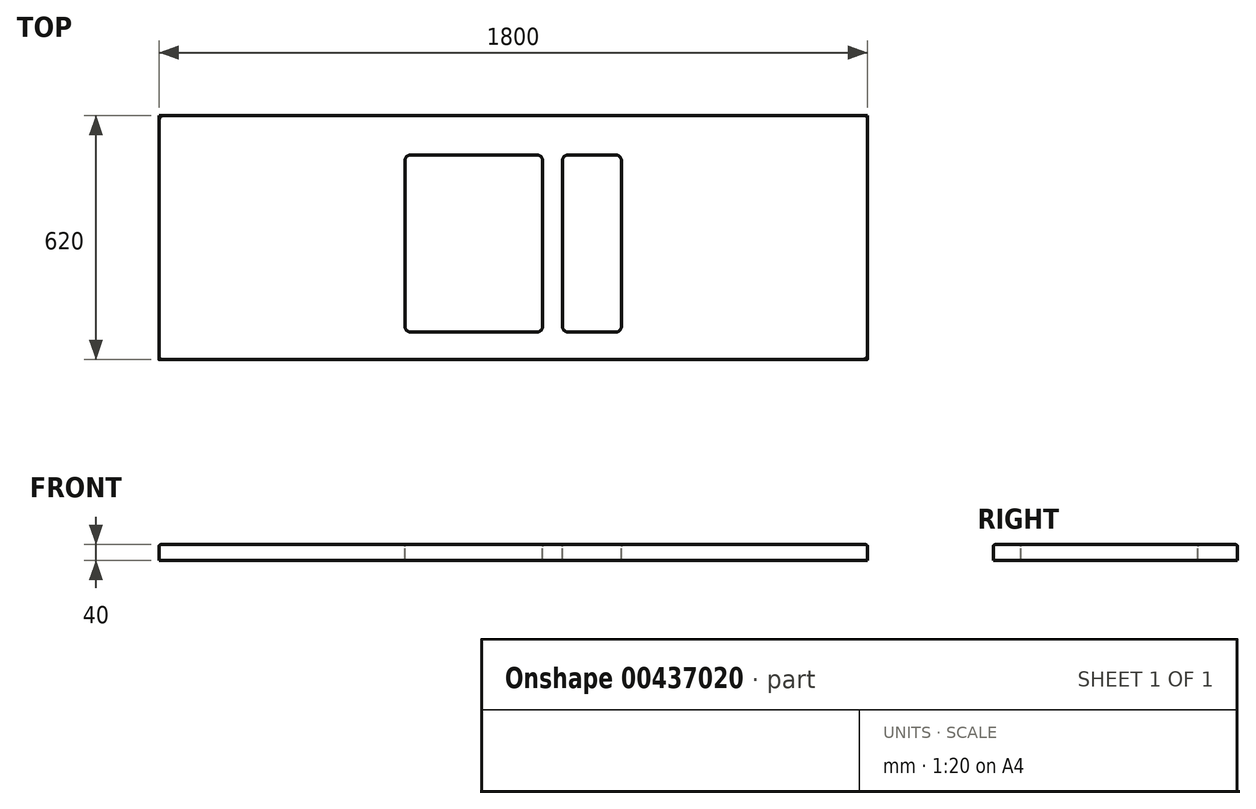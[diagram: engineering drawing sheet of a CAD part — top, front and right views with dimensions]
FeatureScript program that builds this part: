
annotation { "Feature Type Name" : "Feature", "Feature Type Description" : "" }
export const myFeature = defineFeature(function(context is Context, id is Id, definition is map)
    precondition{}
    {
        {
            var Q0;
            Q0=qCreatedBy(makeId("Right.planeOp"),FACE);
            var sketch = newSketch(context, id + "F0", { "sketchPlane" : qUnion([Q0])});
            skLineSegment(sketch, "E0.bottom", {"start": v(0, 0) * mm, "end": v(-620, 0) * mm});
            skLineSegment(sketch, "E0.top", {"start": v(0, 40) * mm, "end": v(-620, 40) * mm});
            skLineSegment(sketch, "E0.left", {"start": v(0, 0) * mm, "end": v(0, 40) * mm});
            skLineSegment(sketch, "E0.right", {"start": v(-620, 0) * mm, "end": v(-620, 40) * mm});
            skSolve(sketch);
        }
        {
            var Q0;
            Q0=qSketchRegion(id+"F0",true);
            extrude(context, id + "F1", {"entities" : qUnion([Q0]), "depth" : 1800 * mm});
        }
        {
            var Q0;
            Q0=makeQuery(id+"F1.opExtrude","SWEPT_FACE",FACE,{"disambiguationData":[OSD([sQuery(id+"F0.wireOp",EDGE,"E0.top")])]});
            var sketch = newSketch(context, id + "F2", { "sketchPlane" : qUnion([Q0])});
            skLineSegment(sketch, "E1.bottom", {"start": v(640, -100) * mm, "end": v(960, -100) * mm});
            skLineSegment(sketch, "E1.top", {"start": v(640, -550) * mm, "end": v(960, -550) * mm});
            skLineSegment(sketch, "E1.left", {"start": v(625, -115) * mm, "end": v(625, -535) * mm});
            skLineSegment(sketch, "E1.right", {"start": v(975, -115) * mm, "end": v(975, -535) * mm});
            skPoint(sketch, "E2.visualSharp", {"position": v(975, -100) * mm});
            skArc(sketch, "E2.filletArc", {"start": v(975, -115) * mm, "mid": v(970.6, -104.4) * mm, "end": v(960, -100) * mm});
            skPoint(sketch, "E3.visualSharp", {"position": v(625, -100) * mm});
            skArc(sketch, "E3.filletArc", {"start": v(640, -100) * mm, "mid": v(629.4, -104.4) * mm, "end": v(625, -115) * mm});
            skPoint(sketch, "E4.visualSharp", {"position": v(625, -550) * mm});
            skArc(sketch, "E4.filletArc", {"start": v(625, -535) * mm, "mid": v(629.4, -545.6) * mm, "end": v(640, -550) * mm});
            skPoint(sketch, "E5.visualSharp", {"position": v(975, -550) * mm});
            skArc(sketch, "E5.filletArc", {"start": v(960, -550) * mm, "mid": v(970.6, -545.6) * mm, "end": v(975, -535) * mm});
            skLineSegment(sketch, "E6.bottom", {"start": v(1040, -100) * mm, "end": v(1160, -100) * mm});
            skLineSegment(sketch, "E6.top", {"start": v(1040, -550) * mm, "end": v(1160, -550) * mm});
            skLineSegment(sketch, "E6.left", {"start": v(1025, -115) * mm, "end": v(1025, -535) * mm});
            skLineSegment(sketch, "E6.right", {"start": v(1175, -115) * mm, "end": v(1175, -535) * mm});
            skPoint(sketch, "E7.visualSharp", {"position": v(1175, -100) * mm});
            skArc(sketch, "E7.filletArc", {"start": v(1175, -115) * mm, "mid": v(1170.6, -104.4) * mm, "end": v(1160, -100) * mm});
            skPoint(sketch, "E8.visualSharp", {"position": v(1025, -100) * mm});
            skArc(sketch, "E8.filletArc", {"start": v(1040, -100) * mm, "mid": v(1029.4, -104.4) * mm, "end": v(1025, -115) * mm});
            skPoint(sketch, "E9.visualSharp", {"position": v(1025, -550) * mm});
            skArc(sketch, "E9.filletArc", {"start": v(1025, -535) * mm, "mid": v(1029.4, -545.6) * mm, "end": v(1040, -550) * mm});
            skPoint(sketch, "E10.visualSharp", {"position": v(1175, -550) * mm});
            skArc(sketch, "E10.filletArc", {"start": v(1160, -550) * mm, "mid": v(1170.6, -545.6) * mm, "end": v(1175, -535) * mm});
            skSolve(sketch);
        }
        {
            var Q0;
            Q0=qSketchRegion(id+"F2",true);
            extrude(context, id + "F3", {"entities" : qUnion([Q0]), "operationType" : NewBodyOperationType.REMOVE, "endBound" : BoundingType.THROUGH_ALL, "oppositeDirection" : true, "depth" : 25 * mm});
        }
        {
            var Q0;
            Q0=makeQuery(id+"F1.opExtrude","SWEPT_FACE",FACE,{"disambiguationData":[OSD([sQuery(id+"F0.wireOp",EDGE,"E0.top")])]});
            fillet(context, id + "F4", {"entities" : qUnion([Q0]), "radius" : 5 * mm, "tangentPropagation" : true, "allowEdgeOverflow" : false});
        }
    });
